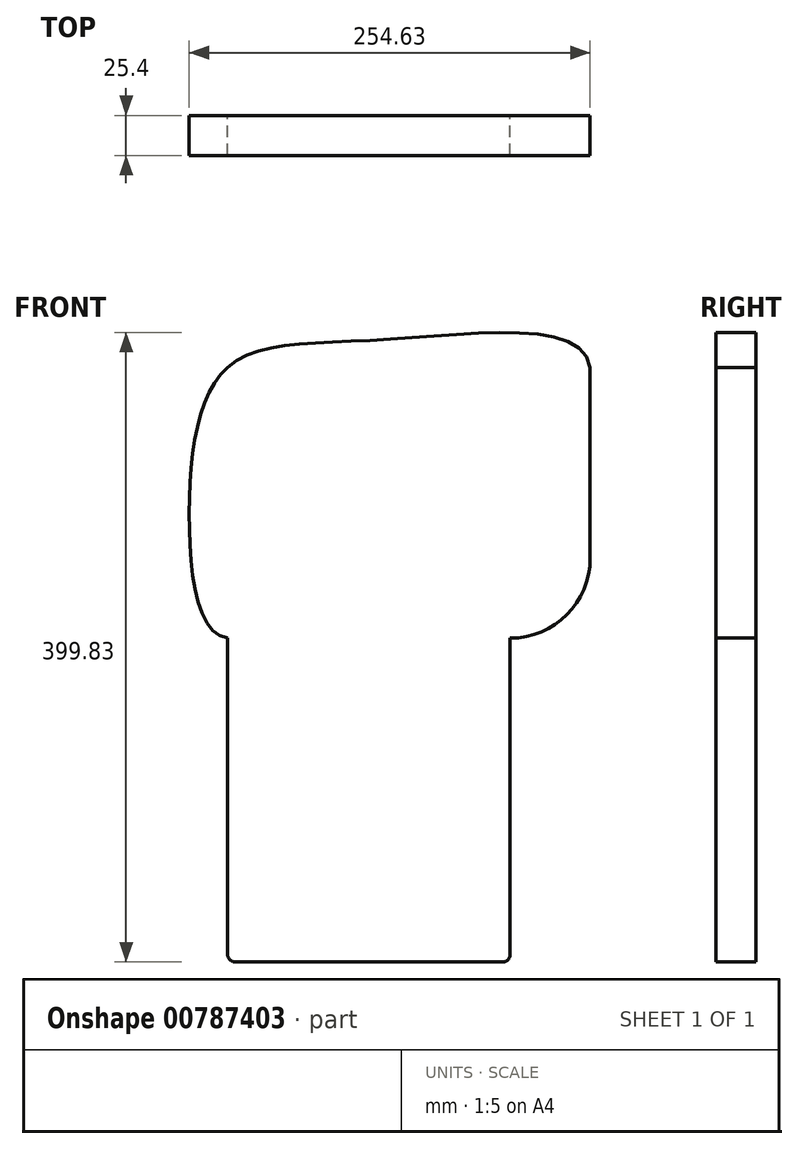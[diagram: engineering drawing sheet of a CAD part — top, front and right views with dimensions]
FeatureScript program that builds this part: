
annotation { "Feature Type Name" : "Feature", "Feature Type Description" : "" }
export const myFeature = defineFeature(function(context is Context, id is Id, definition is map)
    precondition{}
    {
        {
            var Q0;
            Q0=qCreatedBy(makeId("Front.planeOp"),FACE);
            var sketch = newSketch(context, id + "F0", { "sketchPlane" : qUnion([Q0])});
            skLineSegment(sketch, "E0.bottom", {"start": v(-137.87, 77.14) * mm, "end": v(92.4, 77.14) * mm});
            skLineSegment(sketch, "E0.top", {"start": v(-137.87, -94.86) * mm, "end": v(41.6, -94.86) * mm});
            skLineSegment(sketch, "E0.left", {"start": v(-137.87, 77.14) * mm, "end": v(-137.87, -94.86) * mm});
            skLineSegment(sketch, "E0.right", {"start": v(92.4, 77.14) * mm, "end": v(92.4, -44.06) * mm});
            skFitSpline(sketch, "E1", {"points": [v(92.4, 77.14) * mm, v(0, -44.06) * mm, v(-9.48, -33.77) * mm, v(5.21, -10.37) * mm, v(24.34, 26.08) * mm, v(-22.44, 40.75) * mm, v(-46.1, -7.35) * mm, v(-137.87, -94.86) * mm, v(-162.2, -13.7) * mm, v(-137.87, 77.14) * mm, v(-36.86, 94.87) * mm, v(92.4, 77.14) * mm]});
            skPoint(sketch, "E2.visualSharp", {"position": v(92.4, -94.86) * mm});
            skArc(sketch, "E2.filletArc", {"start": v(41.6, -94.86) * mm, "mid": v(77.53, -79.99) * mm, "end": v(92.4, -44.06) * mm});
            skSolve(sketch);
        }
        {
            var Q0;
            {var subQ0=sQuery(id+"F0.wireOp",EDGE,"E0.left");Q0=makeQuery(id+"F0.imprint","IMPRINT",FACE,{"disambiguationData":[TD([[makeQuery(id+"F0.imprint","IMPRINT",EDGE,{"derivedFrom":subQ0}),-1.0]])]});}
            var Q1;
            {var subQ0=sQuery(id+"F0.wireOp",EDGE,"E0.bottom");Q1=makeQuery(id+"F0.imprint","IMPRINT",FACE,{"disambiguationData":[TD([[makeQuery(id+"F0.imprint","IMPRINT",EDGE,{"derivedFrom":subQ0}),1.0]])]});}
            var Q2;
            {var subQ0=sQuery(id+"F0.wireOp",EDGE,"E0.top");Q2=makeQuery(id+"F0.imprint","IMPRINT",FACE,{"disambiguationData":[TD([[makeQuery(id+"F0.imprint","IMPRINT",EDGE,{"derivedFrom":subQ0}),1.0]])]});}
            var Q3;
            {var subQ0=sQuery(id+"F0.wireOp",EDGE,"E0.bottom");Q3=makeQuery(id+"F0.imprint","IMPRINT",FACE,{"disambiguationData":[TD([[makeQuery(id+"F0.imprint","IMPRINT",EDGE,{"derivedFrom":subQ0}),-1.0]])]});}
            extrude(context, id + "F1", {"entities" : qUnion([Q0, Q1, Q2, Q3]), "depth" : 25.4 * mm, "offsetDistance" : 25.4 * mm});
        }
        {
            var Q0;
            Q0=makeQuery(id+"F1.opExtrude","SWEPT_FACE",FACE,{"disambiguationData":[OSD([sQuery(id+"F0.wireOp",EDGE,"E0.top")])]});
            extrude(context, id + "F2", {"entities" : qUnion([Q0]), "operationType" : NewBodyOperationType.ADD, "depth" : 205.74 * mm, "offsetDistance" : 25.4 * mm});
        }
        {
            var Q0;
            Q0=makeQuery(id+"F2.opExtrude","CAP_EDGE",EDGE,{"disambiguationData":[OSD([sQuery(id+"F0.wireOp",EDGE,"E0.top"),sQuery(id+"F0.wireOp",EDGE,"E2.filletArc")])],"isStart":false});
            var Q1;
            Q1=makeQuery(id+"F2.opExtrude","CAP_EDGE",EDGE,{"disambiguationData":[OSD([sQuery(id+"F0.wireOp",EDGE,"E0.top"),sQuery(id+"F0.wireOp",EDGE,"E0.left"),sQuery(id+"F0.wireOp",EDGE,"E1")])],"isStart":false});
            fillet(context, id + "F3", {"entities" : qUnion([Q0, Q1]), "radius" : 5.08 * mm, "tangentPropagation" : true, "allowEdgeOverflow" : false});
        }
    });
